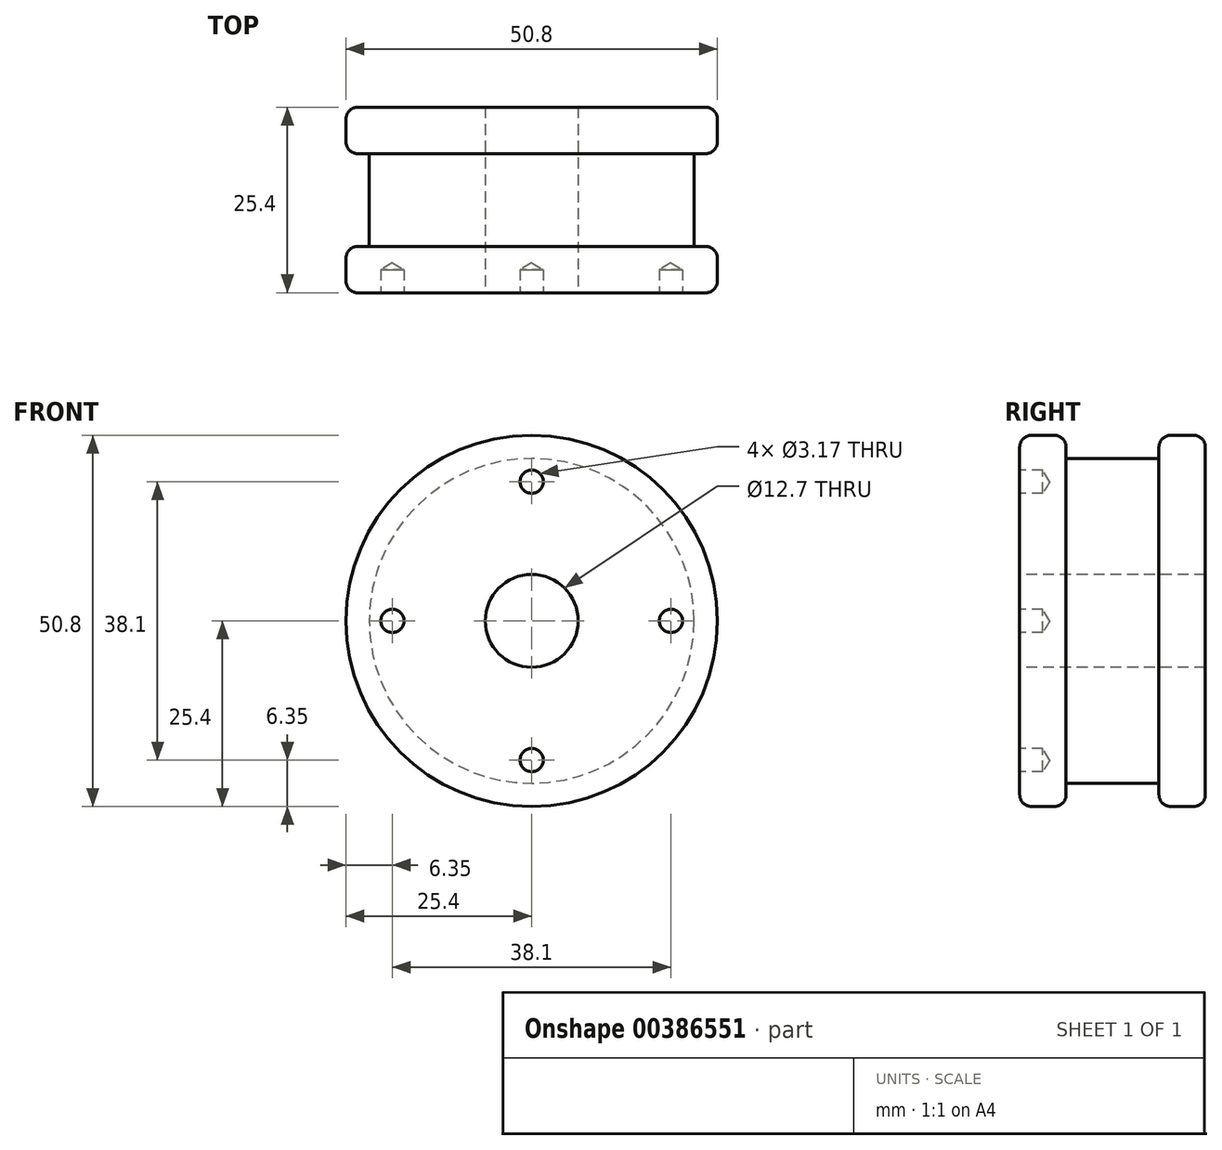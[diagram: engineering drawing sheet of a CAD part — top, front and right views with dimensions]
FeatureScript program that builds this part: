
annotation { "Feature Type Name" : "Feature", "Feature Type Description" : "" }
export const myFeature = defineFeature(function(context is Context, id is Id, definition is map)
    precondition{}
    {
        {
            var Q0;
            Q0=qCreatedBy(makeId("Front.planeOp"),FACE);
            var sketch = newSketch(context, id + "F0", { "sketchPlane" : qUnion([Q0])});
            skCircle(sketch, "E0", {"center": v(0, 0) * mm, "radius": 25.4 * mm});
            skSolve(sketch);
        }
        {
            var Q0;
            Q0 = qSketchRegion(id + "F0", true);
            extrude(context, id + "F1", {"entities" : qUnion([Q0]), "depth" : 6.35 * mm});
        }
        {
            var Q0;
            Q0=makeQuery(id+"F1.opExtrude","CAP_FACE",FACE,{"disambiguationData":[OSD([sQuery(id+"F0.wireOp",EDGE,"E0")])],"isStart":false});
            var sketch = newSketch(context, id + "F2", { "sketchPlane" : qUnion([Q0])});
            skCircle(sketch, "E1", {"center": v(0, 0) * mm, "radius": 22.23 * mm});
            skSolve(sketch);
        }
        {
            var Q0;
            Q0 = qSketchRegion(id + "F2", true);
            extrude(context, id + "F3", {"entities" : qUnion([Q0]), "operationType" : NewBodyOperationType.ADD, "depth" : 12.7 * mm});
        }
        {
            var Q0;
            Q0=makeQuery(id+"F3.opExtrude","CAP_FACE",FACE,{"disambiguationData":[OSD([sQuery(id+"F2.wireOp",EDGE,"E1")])],"isStart":false});
            var sketch = newSketch(context, id + "F4", { "sketchPlane" : qUnion([Q0])});
            skCircle(sketch, "E2", {"center": v(0, 0) * mm, "radius": 25.4 * mm});
            skSolve(sketch);
        }
        {
            var Q0;
            Q0 = qSketchRegion(id + "F4", true);
            extrude(context, id + "F5", {"entities" : qUnion([Q0]), "operationType" : NewBodyOperationType.ADD, "depth" : 6.35 * mm});
        }
        {
            var Q0;
            Q0=makeQuery(id+"F5.opExtrude","CAP_FACE",FACE,{"disambiguationData":[OSD([sQuery(id+"F4.wireOp",EDGE,"E2")])],"isStart":false});
            var sketch = newSketch(context, id + "F6", { "sketchPlane" : qUnion([Q0])});
            skCircle(sketch, "E3", {"center": v(0, 0) * mm, "radius": 6.35 * mm});
            skSolve(sketch);
        }
        {
            var Q0;
            Q0=sQuery(id+"F6.wireOp",VERTEX,"E3.center");
            var Q1;
            Q1=makeQuery(id+"F1.opExtrude","SWEPT_BODY",BODY,{"disambiguationData":[OSD([sQuery(id+"F0.wireOp",EDGE,"E0")])]});
            hole(context, id + "F7", {"style" : HoleStyle.SIMPLE, "endStyle" : HoleEndStyle.THROUGH, "holeDiameter" : 12.7 * mm, "isTappedThrough" : true, "tappedDepth" : 12.7 * mm, "tapClearance" : 3, "locations" : qUnion([Q0]), "scope" : qUnion([Q1])});
        }
        {
            var Q0;
            Q0=makeQuery(id+"F5.opExtrude","CAP_FACE",FACE,{"disambiguationData":[OSD([sQuery(id+"F4.wireOp",EDGE,"E2")])],"isStart":false});
            var sketch = newSketch(context, id + "F8", { "sketchPlane" : qUnion([Q0])});
            skPoint(sketch, "E4", {"position": v(0, 19.05) * mm});
            skPoint(sketch, "E5", {"position": v(-19.05, 0) * mm});
            skPoint(sketch, "E6", {"position": v(0, -19.05) * mm});
            skPoint(sketch, "E7", {"position": v(19.05, 0) * mm});
            skSolve(sketch);
        }
        {
            var Q0;
            Q0=sQuery(id+"F8.wireOp",VERTEX,"E4");
            var Q1;
            Q1=sQuery(id+"F8.wireOp",VERTEX,"E7");
            var Q2;
            Q2=sQuery(id+"F8.wireOp",VERTEX,"E6");
            var Q3;
            Q3=sQuery(id+"F8.wireOp",VERTEX,"E5");
            var Q4;
            Q4=makeQuery(id+"F1.opExtrude","SWEPT_BODY",BODY,{"disambiguationData":[OSD([sQuery(id+"F0.wireOp",EDGE,"E0")])]});
            hole(context, id + "F9", {"style" : HoleStyle.SIMPLE, "endStyle" : HoleEndStyle.BLIND, "holeDiameter" : 3.17 * mm, "holeDepth" : 3.17 * mm, "isTappedThrough" : true, "tappedDepth" : 12.7 * mm, "tapClearance" : 3, "locations" : qUnion([Q0, Q1, Q2, Q3]), "scope" : qUnion([Q4])});
        }
        {
            var Q0;
            Q0=makeQuery(id+"F5.opExtrude","CAP_EDGE",EDGE,{"disambiguationData":[OSD([sQuery(id+"F4.wireOp",EDGE,"E2")])],"isStart":false});
            var Q1;
            Q1=makeQuery(id+"F5.opExtrude","CAP_EDGE",EDGE,{"disambiguationData":[OSD([sQuery(id+"F4.wireOp",EDGE,"E2")])],"isStart":true});
            var Q2;
            Q2=makeQuery(id+"F1.opExtrude","CAP_EDGE",EDGE,{"disambiguationData":[OSD([sQuery(id+"F0.wireOp",EDGE,"E0")])],"isStart":false});
            var Q3;
            Q3=makeQuery(id+"F1.opExtrude","CAP_EDGE",EDGE,{"disambiguationData":[OSD([sQuery(id+"F0.wireOp",EDGE,"E0")])],"isStart":true});
            fillet(context, id + "F10", {"entities" : qUnion([Q0, Q1, Q2, Q3]), "radius" : 1.6 * mm, "tangentPropagation" : true, "allowEdgeOverflow" : false});
        }
    });
